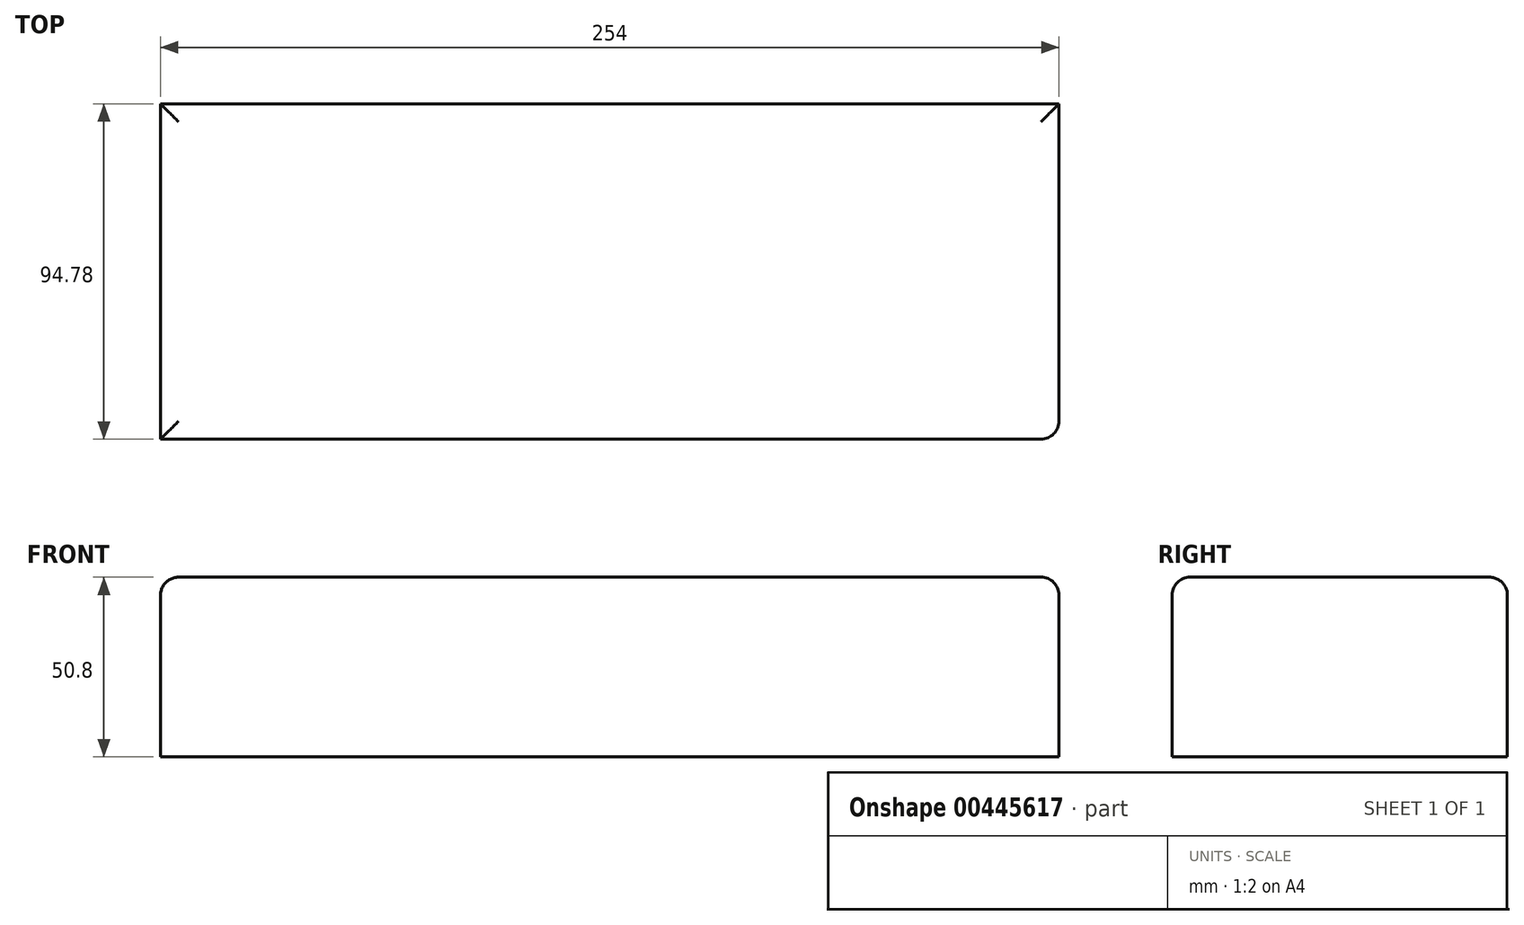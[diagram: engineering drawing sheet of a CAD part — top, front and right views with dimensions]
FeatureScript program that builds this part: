
annotation { "Feature Type Name" : "Feature", "Feature Type Description" : "" }
export const myFeature = defineFeature(function(context is Context, id is Id, definition is map)
    precondition{}
    {
        {
            var Q0;
            Q0=qCreatedBy(makeId("Top.planeOp"),FACE);
            var sketch = newSketch(context, id + "F0", { "sketchPlane" : qUnion([Q0])});
            skLineSegment(sketch, "E0.bottom", {"start": v(127, 47.39) * mm, "end": v(-127, 47.39) * mm});
            skLineSegment(sketch, "E0.top", {"start": v(127, -47.39) * mm, "end": v(-127, -47.39) * mm});
            skLineSegment(sketch, "E0.left", {"start": v(127, 47.39) * mm, "end": v(127, -47.39) * mm});
            skLineSegment(sketch, "E0.right", {"start": v(-127, 47.39) * mm, "end": v(-127, -47.39) * mm});
            skPoint(sketch, "E0.middle", {"position": v(0, 0) * mm});
            skSolve(sketch);
        }
        {
            var Q0;
            Q0 = qSketchRegion(id + "F0", true);
            extrude(context, id + "F1", {"entities" : qUnion([Q0]), "depth" : 50.8 * mm});
        }
        {
            var Q0;
            Q0=makeQuery(id+"F1.opExtrude","CAP_EDGE",EDGE,{"disambiguationData":[OSD([sQuery(id+"F0.wireOp",EDGE,"E0.top")])],"isStart":false});
            var Q1;
            Q1=makeQuery(id+"F1.opExtrude","CAP_EDGE",EDGE,{"disambiguationData":[OSD([sQuery(id+"F0.wireOp",EDGE,"E0.left")])],"isStart":false});
            var Q2;
            Q2=makeQuery(id+"F1.opExtrude","CAP_EDGE",EDGE,{"disambiguationData":[OSD([sQuery(id+"F0.wireOp",EDGE,"E0.bottom")])],"isStart":false});
            var Q3;
            Q3=makeQuery(id+"F1.opExtrude","CAP_EDGE",EDGE,{"disambiguationData":[OSD([sQuery(id+"F0.wireOp",EDGE,"E0.right")])],"isStart":false});
            var Q4;
            Q4=makeQuery(id+"F1.opExtrude","SWEPT_EDGE",EDGE,{"disambiguationData":[OSD([sQuery(id+"F0.wireOp",EDGE,"E0.top"),sQuery(id+"F0.wireOp",EDGE,"E0.left")])]});
            fillet(context, id + "F2", {"entities" : qUnion([Q0, Q1, Q2, Q3, Q4]), "radius" : 5.08 * mm, "tangentPropagation" : true, "allowEdgeOverflow" : false});
        }
    });
